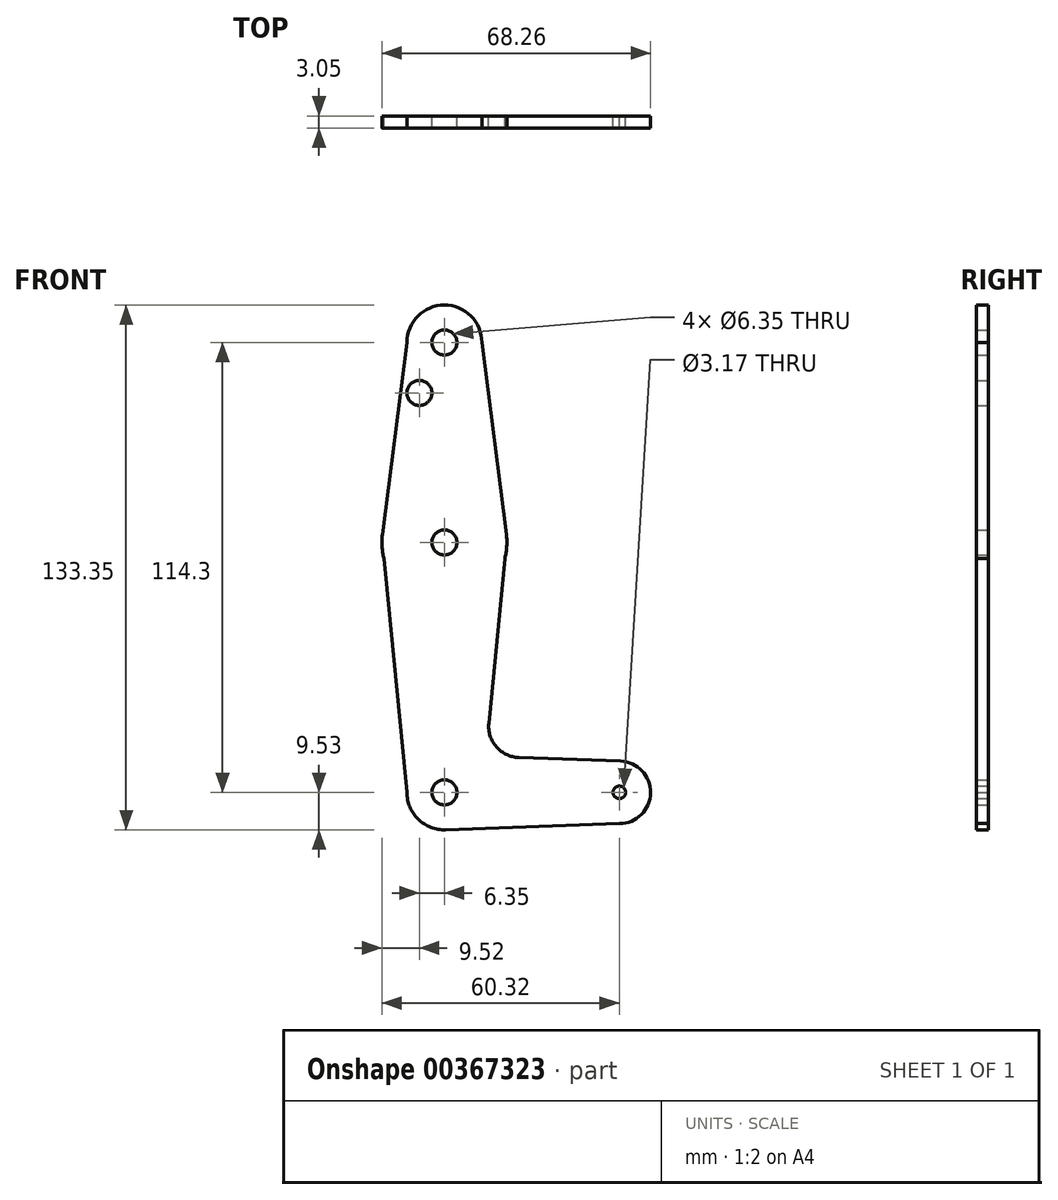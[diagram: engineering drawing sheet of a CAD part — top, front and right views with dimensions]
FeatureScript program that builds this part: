
annotation { "Feature Type Name" : "Feature", "Feature Type Description" : "" }
export const myFeature = defineFeature(function(context is Context, id is Id, definition is map)
    precondition{}
    {
        {
            var Q0;
            Q0=qCreatedBy(makeId("Front.planeOp"),FACE);
            var sketch = newSketch(context, id + "F0", { "sketchPlane" : qUnion([Q0])});
            skCircle(sketch, "E0", {"center": v(0, 50.8) * mm, "radius": 9.53 * mm});
            skCircle(sketch, "E1", {"center": v(0, 0) * mm, "radius": 15.88 * mm});
            skCircle(sketch, "E2", {"center": v(0, -63.5) * mm, "radius": 9.53 * mm});
            skCircle(sketch, "E3", {"center": v(44.45, -63.5) * mm, "radius": 7.94 * mm});
            skLineSegment(sketch, "E4", {"start": v(0, 50.8) * mm, "end": v(0, -63.5) * mm, "construction": true});
            skLineSegment(sketch, "E5", {"start": v(44.45, -63.5) * mm, "end": v(0, -63.5) * mm, "construction": true});
            skLineSegment(sketch, "E6", {"start": v(-9.53, 50.8) * mm, "end": v(-15.75, 2) * mm});
            skLineSegment(sketch, "E7", {"start": v(9.53, 50.8) * mm, "end": v(15.75, 2) * mm});
            skLineSegment(sketch, "E8", {"start": v(44.45, -71.44) * mm, "end": v(0, -73.03) * mm});
            skCircle(sketch, "E9", {"center": v(0, 50.8) * mm, "radius": 3.17 * mm});
            skCircle(sketch, "E10", {"center": v(-6.35, 38) * mm, "radius": 3.18 * mm});
            skCircle(sketch, "E11", {"center": v(0, 0) * mm, "radius": 3.17 * mm});
            skCircle(sketch, "E12", {"center": v(44.45, -63.5) * mm, "radius": 1.59 * mm});
            skLineSegment(sketch, "E13", {"start": v(-9.53, -63.5) * mm, "end": v(9.57, -63.5) * mm});
            skLineSegment(sketch, "E14", {"start": v(-15.75, 0) * mm, "end": v(-9.53, -63.5) * mm});
            skLineSegment(sketch, "E15", {"start": v(15.75, 0) * mm, "end": v(11.28, -45.93) * mm});
            skLineSegment(sketch, "E16", {"start": v(18.91, -54.65) * mm, "end": v(44.73, -55.57) * mm});
            skArc(sketch, "E17.filletArc", {"start": v(11.28, -45.93) * mm, "mid": v(13.21, -51.94) * mm, "end": v(18.91, -54.65) * mm});
            skCircle(sketch, "E18", {"center": v(0, -63.5) * mm, "radius": 3.18 * mm});
            skSolve(sketch);
        }
        {
            var Q0;
            Q0 = qSketchRegion(id + "F0", true);
            extrude(context, id + "F1", {"entities" : qUnion([Q0]), "depth" : 3.05 * mm});
        }
    });
